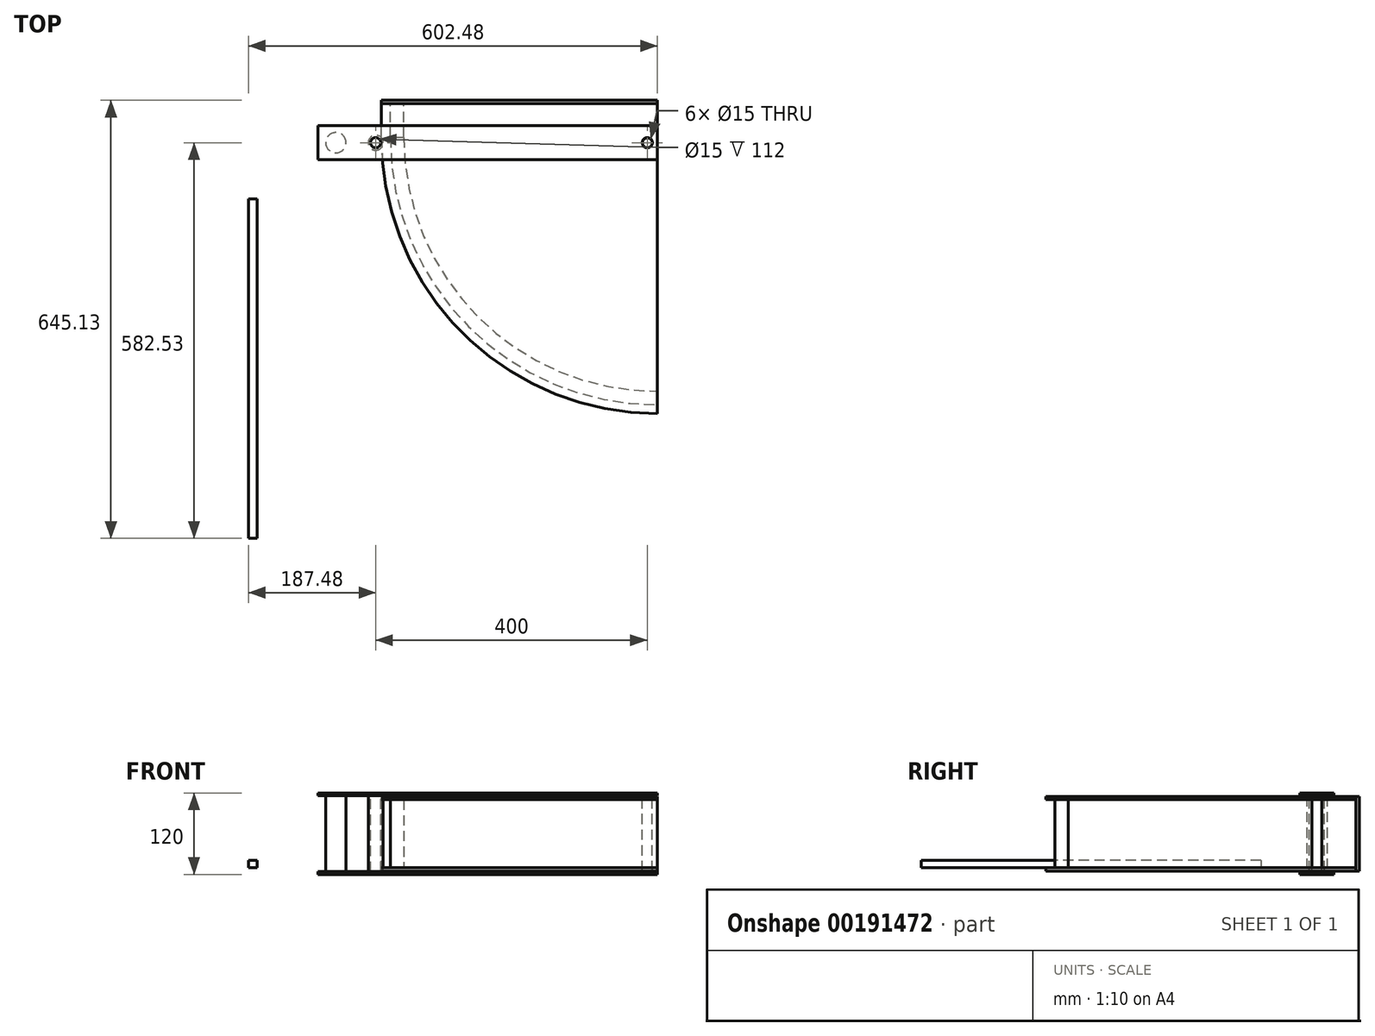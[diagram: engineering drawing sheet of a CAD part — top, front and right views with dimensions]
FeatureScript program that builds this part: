
annotation { "Feature Type Name" : "Feature", "Feature Type Description" : "" }
export const myFeature = defineFeature(function(context is Context, id is Id, definition is map)
    precondition{}
    {
        {
            var Q0;
            Q0=qCreatedBy(makeId("Top.planeOp"),FACE);
            var sketch = newSketch(context, id + "F0", { "sketchPlane" : qUnion([Q0])});
            skLineSegment(sketch, "E0", {"start": v(0, 0) * mm, "end": v(-393.5, 0) * mm});
            skArc(sketch, "E1", {"start": v(-393.5, 0) * mm, "mid": v(-278.25, -278.25) * mm, "end": v(0, -393.5) * mm});
            skLineSegment(sketch, "E2", {"start": v(0, 0) * mm, "end": v(0, -393.5) * mm});
            skArc(sketch, "E3.0", {"start": v(-373.5, 0) * mm, "mid": v(-264.1, -264.1) * mm, "end": v(0, -373.5) * mm});
            skLineSegment(sketch, "E4.top", {"start": v(-393.5, 50) * mm, "end": v(-373.5, 50) * mm});
            skLineSegment(sketch, "E4.left", {"start": v(-393.5, 0) * mm, "end": v(-393.5, 50) * mm});
            skLineSegment(sketch, "E4.right", {"start": v(-373.5, 0) * mm, "end": v(-373.5, 50) * mm});
            skSolve(sketch);
        }
        {
            var Q0;
            {var subQ0=sQuery(id+"F0.wireOp",EDGE,"E1");Q0=makeQuery(id+"F0.imprint","IMPRINT",FACE,{"disambiguationData":[TD([[makeQuery(id+"F0.imprint","IMPRINT",EDGE,{"derivedFrom":subQ0}),1.0]])]});}
            var Q1;
            Q1=makeQuery(id+"F0.imprint","IMPRINT",FACE,{"disambiguationData":[TD([[makeQuery(id+"F0.imprint","IMPRINT",EDGE,{"derivedFrom":sQuery(id+"F0.wireOp",EDGE,"E4.bottom")}),1.0]])]});
            extrude(context, id + "F1", {"entities" : qUnion([Q0, Q1]), "depth" : 100 * mm});
        }
        {
            var Q0;
            Q0=makeQuery(id+"F1.opExtrude","CAP_FACE",FACE,{"disambiguationData":[OSD([sQuery(id+"F0.wireOp",EDGE,"E0"),sQuery(id+"F0.wireOp",EDGE,"E1"),sQuery(id+"F0.wireOp",EDGE,"E2"),sQuery(id+"F0.wireOp",EDGE,"E3.0")])],"isStart":true});
            cPlane(context, id + "F2", {"entities" : qUnion([Q0]), "cplaneType" : CPlaneType.OFFSET, "offset" : 0 * mm, "width" : 150 * mm, "height" : 150 * mm});
        }
        {
            var Q0;
            Q0=qCreatedBy(id+"F2.planeOp",FACE);
            var sketch = newSketch(context, id + "F3", { "sketchPlane" : qUnion([Q0])});
            skLineSegment(sketch, "E5", {"start": v(0, 0) * mm, "end": v(0, 406.5) * mm});
            skLineSegment(sketch, "E6", {"start": v(0, 0) * mm, "end": v(-406.5, 0) * mm});
            skArc(sketch, "E7", {"start": v(0, 393.5) * mm, "mid": v(-278.25, 278.25) * mm, "end": v(-393.5, 0) * mm});
            skArc(sketch, "E8.0", {"start": v(0, 406.5) * mm, "mid": v(-287.44, 287.44) * mm, "end": v(-406.5, 0) * mm});
            skLineSegment(sketch, "E9.bottom", {"start": v(-406.5, 0) * mm, "end": v(0, 0) * mm});
            skLineSegment(sketch, "E9.top", {"start": v(-406.5, -50) * mm, "end": v(0, -50) * mm});
            skLineSegment(sketch, "E9.right", {"start": v(0, 0) * mm, "end": v(0, -50) * mm});
            skLineSegment(sketch, "E10", {"start": v(-406.5, 0) * mm, "end": v(-406.5, -50) * mm});
            skSolve(sketch);
        }
        {
            var Q0;
            Q0=qSketchRegion(id+"F3",true);
            extrude(context, id + "F4", {"entities" : qUnion([Q0]), "depth" : 5 * mm});
        }
        {
            var Q0;
            Q0=makeQuery(id+"F1.opExtrude","CAP_FACE",FACE,{"disambiguationData":[OSD([sQuery(id+"F0.wireOp",EDGE,"E0"),sQuery(id+"F0.wireOp",EDGE,"E1"),sQuery(id+"F0.wireOp",EDGE,"E2"),sQuery(id+"F0.wireOp",EDGE,"E3.0")])],"isStart":false});
            cPlane(context, id + "F5", {"entities" : qUnion([Q0]), "cplaneType" : CPlaneType.OFFSET, "offset" : 0 * mm, "width" : 150 * mm, "height" : 150 * mm});
        }
        {
            var Q0;
            Q0=qCreatedBy(id+"F5.planeOp",FACE);
            var sketch = newSketch(context, id + "F6", { "sketchPlane" : qUnion([Q0])});
            skLineSegment(sketch, "E11", {"start": v(0, 0) * mm, "end": v(0, -393.5) * mm});
            skLineSegment(sketch, "E12", {"start": v(0, 0) * mm, "end": v(-393.5, 0) * mm});
            skArc(sketch, "E13.0", {"start": v(-393.5, 0) * mm, "mid": v(-278.25, -278.25) * mm, "end": v(0, -393.5) * mm});
            skLineSegment(sketch, "E14.bottom", {"start": v(-393.5, 0) * mm, "end": v(0, 0) * mm});
            skLineSegment(sketch, "E14.top", {"start": v(-393.5, 50) * mm, "end": v(0, 50) * mm});
            skLineSegment(sketch, "E14.left", {"start": v(-393.5, 0) * mm, "end": v(-393.5, 50) * mm});
            skLineSegment(sketch, "E14.right", {"start": v(0, 0) * mm, "end": v(0, 50) * mm});
            skLineSegment(sketch, "E15", {"start": v(0, -393.5) * mm, "end": v(0, -406.5) * mm});
            skArc(sketch, "E16", {"start": v(-406.5, 0) * mm, "mid": v(-287.44, -287.44) * mm, "end": v(0, -406.5) * mm});
            skLineSegment(sketch, "E17", {"start": v(-393.5, 0) * mm, "end": v(-406.5, 0) * mm});
            skLineSegment(sketch, "E18", {"start": v(-406.5, 0) * mm, "end": v(-406.5, 50) * mm});
            skLineSegment(sketch, "E19", {"start": v(-406.5, 50) * mm, "end": v(-393.5, 50) * mm});
            skSolve(sketch);
        }
        {
            var Q0;
            Q0=qSketchRegion(id+"F6",true);
            extrude(context, id + "F7", {"entities" : qUnion([Q0]), "depth" : 5 * mm});
        }
        {
            var Q0;
            Q0=makeQuery(id+"F4.opExtrude","SWEPT_FACE",FACE,{"disambiguationData":[OSD([sQuery(id+"F3.wireOp",EDGE,"E9.top")])]});
            cPlane(context, id + "F8", {"entities" : qUnion([Q0]), "cplaneType" : CPlaneType.OFFSET, "offset" : 0 * mm, "width" : 150 * mm, "height" : 150 * mm});
        }
        {
            var Q0;
            Q0=qCreatedBy(id+"F8.planeOp",FACE);
            var sketch = newSketch(context, id + "F9", { "sketchPlane" : qUnion([Q0])});
            skLineSegment(sketch, "E20", {"start": v(0, -5) * mm, "end": v(0, 105) * mm});
            skLineSegment(sketch, "E21", {"start": v(0, -5) * mm, "end": v(406.5, -5) * mm});
            skLineSegment(sketch, "E22", {"start": v(406.5, -5) * mm, "end": v(406.5, 105) * mm});
            skLineSegment(sketch, "E23", {"start": v(406.5, 105) * mm, "end": v(0, 105) * mm});
            skSolve(sketch);
        }
        {
            var Q0;
            Q0=qSketchRegion(id+"F9",true);
            extrude(context, id + "F10", {"entities" : qUnion([Q0]), "depth" : 5.1 * mm});
        }
        {
            var Q0;
            Q0=makeQuery(id+"F7.opExtrude","CAP_FACE",FACE,{"disambiguationData":[OSD([sQuery(id+"F6.wireOp",EDGE,"E11"),sQuery(id+"F6.wireOp",EDGE,"E13.0"),sQuery(id+"F6.wireOp",EDGE,"E14.top"),sQuery(id+"F6.wireOp",EDGE,"E14.left"),sQuery(id+"F6.wireOp",EDGE,"E14.right")])],"isStart":false});
            var sketch = newSketch(context, id + "F11", { "sketchPlane" : qUnion([Q0])});
            skCircle(sketch, "E24", {"center": v(-15, -7.5) * mm, "radius": 7.5 * mm});
            skSolve(sketch);
        }
        {
            var Q0;
            Q0=qSketchRegion(id+"F11",true);
            extrude(context, id + "F12", {"entities" : qUnion([Q0]), "operationType" : NewBodyOperationType.REMOVE, "endBound" : BoundingType.THROUGH_ALL, "oppositeDirection" : true, "depth" : 42 * mm});
        }
        {
            var Q0;
            Q0=makeQuery(id+"F7.opExtrude","CAP_FACE",FACE,{"disambiguationData":[OSD([sQuery(id+"F6.wireOp",EDGE,"E11"),sQuery(id+"F6.wireOp",EDGE,"E13.0"),sQuery(id+"F6.wireOp",EDGE,"E14.top"),sQuery(id+"F6.wireOp",EDGE,"E14.left"),sQuery(id+"F6.wireOp",EDGE,"E14.right")])],"isStart":false});
            cPlane(context, id + "F13", {"entities" : qUnion([Q0]), "cplaneType" : CPlaneType.OFFSET, "offset" : 5 * mm, "width" : 150 * mm, "height" : 150 * mm});
        }
        {
            var Q0;
            Q0=qCreatedBy(id+"F13.planeOp",FACE);
            var sketch = newSketch(context, id + "F14", { "sketchPlane" : qUnion([Q0])});
            skCircle(sketch, "E25", {"center": v(-15, -7.5) * mm, "radius": 7.25 * mm});
            skSolve(sketch);
        }
        {
            var Q0;
            Q0=qSketchRegion(id+"F14",true);
            extrude(context, id + "F15", {"entities" : qUnion([Q0]), "oppositeDirection" : true, "depth" : 120 * mm});
        }
        {
            var Q0;
            Q0=makeQuery(id+"F15.opExtrude","CAP_FACE",FACE,{"disambiguationData":[OSD([sQuery(id+"F14.wireOp",EDGE,"E25")])],"isStart":true});
            cPlane(context, id + "F16", {"entities" : qUnion([Q0]), "cplaneType" : CPlaneType.OFFSET, "offset" : 0 * mm, "width" : 150 * mm, "height" : 150 * mm});
        }
        {
            var Q0;
            Q0=qCreatedBy(id+"F16.planeOp",FACE);
            var sketch = newSketch(context, id + "F17", { "sketchPlane" : qUnion([Q0])});
            skLineSegment(sketch, "E26.bottom", {"start": v(0, -32.5) * mm, "end": v(-500, -32.5) * mm});
            skLineSegment(sketch, "E26.top", {"start": v(0, 17.5) * mm, "end": v(-500, 17.5) * mm});
            skLineSegment(sketch, "E26.left", {"start": v(0, -32.5) * mm, "end": v(0, 17.5) * mm});
            skLineSegment(sketch, "E26.right", {"start": v(-500, -32.5) * mm, "end": v(-500, 17.5) * mm});
            skCircle(sketch, "E27", {"center": v(-15, -7.5) * mm, "radius": 7.5 * mm});
            skCircle(sketch, "E28", {"center": v(-415, -7.5) * mm, "radius": 7.5 * mm});
            skSolve(sketch);
        }
        {
            var Q0;
            Q0=qSketchRegion(id+"F17",true);
            extrude(context, id + "F18", {"entities" : qUnion([Q0]), "operationType" : NewBodyOperationType.ADD, "oppositeDirection" : true, "depth" : 4 * mm});
        }
        {
            var Q0;
            Q0=qCreatedBy(id+"F5.planeOp",FACE);
            cPlane(context, id + "F19", {"entities" : qUnion([Q0]), "cplaneType" : CPlaneType.OFFSET, "offset" : 50 * mm, "oppositeDirection" : true, "width" : 150 * mm, "height" : 150 * mm});
        }
        {
            var Q0;
            Q0=makeQuery(id+"F18.opExtrude","SWEPT_BODY",BODY,{"disambiguationData":[OSD([sQuery(id+"F17.wireOp",EDGE,"E26.bottom"),sQuery(id+"F17.wireOp",EDGE,"E26.top"),sQuery(id+"F17.wireOp",EDGE,"E26.left"),sQuery(id+"F17.wireOp",EDGE,"E26.right"),sQuery(id+"F17.wireOp",EDGE,"E27")])]});
            var Q1;
            Q1=qCreatedBy(id+"F19.planeOp",FACE);
            mirror(context, id + "F20", {"entities" : qUnion([Q0]), "mirrorPlane" : qUnion([Q1])});
        }
        {
            var Q0;
            Q0=makeQuery(id+"F0.imprint","IMPRINT",FACE,{"disambiguationData":[TD([[makeQuery(id+"F0.imprint","IMPRINT",EDGE,{"derivedFrom":sQuery(id+"F0.wireOp",EDGE,"E4.top")}),-1.0]])]});
            extrude(context, id + "F21", {"entities" : qUnion([Q0]), "depth" : 100 * mm});
        }
        {
            var Q0;
            Q0=makeQuery(id+"F20.opPattern","COPY",FACE,{"derivedFrom":makeQuery(id+"F18.opExtrude","CAP_FACE",FACE,{"disambiguationData":[OSD([sQuery(id+"F17.wireOp",EDGE,"E26.bottom"),sQuery(id+"F17.wireOp",EDGE,"E26.top"),sQuery(id+"F17.wireOp",EDGE,"E26.left"),sQuery(id+"F17.wireOp",EDGE,"E26.right"),sQuery(id+"F17.wireOp",EDGE,"E27"),sQuery(id+"F17.wireOp",EDGE,"E28")])],"isStart":false}),"instanceName":"1"});
            var sketch = newSketch(context, id + "F22", { "sketchPlane" : qUnion([Q0])});
            skCircle(sketch, "E29", {"center": v(-473.58, -7.5) * mm, "radius": 15 * mm});
            skPoint(sketch, "E29.centerSnap0", {"position": v(-500, -7.5) * mm});
            skSolve(sketch);
        }
        {
            var Q0;
            Q0=qSketchRegion(id+"F22",true);
            extrude(context, id + "F23", {"entities" : qUnion([Q0]), "endBound" : BoundingType.UP_TO_NEXT, "depth" : 25 * mm});
        }
        {
            var Q0;
            Q0=makeQuery(id+"F18.opExtrude","CAP_FACE",FACE,{"disambiguationData":[OSD([sQuery(id+"F17.wireOp",EDGE,"E26.bottom"),sQuery(id+"F17.wireOp",EDGE,"E26.top"),sQuery(id+"F17.wireOp",EDGE,"E26.left"),sQuery(id+"F17.wireOp",EDGE,"E26.right"),sQuery(id+"F17.wireOp",EDGE,"E27"),sQuery(id+"F17.wireOp",EDGE,"E28")])],"isStart":false});
            var sketch = newSketch(context, id + "F24", { "sketchPlane" : qUnion([Q0])});
            skCircle(sketch, "E30", {"center": v(-415, 7.5) * mm, "radius": 7.5 * mm});
            skCircle(sketch, "E31", {"center": v(-415, 7.5) * mm, "radius": 11 * mm});
            skSolve(sketch);
        }
        {
            var Q0;
            Q0=qSketchRegion(id+"F24",true);
            extrude(context, id + "F25", {"entities" : qUnion([Q0]), "endBound" : BoundingType.UP_TO_NEXT, "depth" : 25 * mm});
        }
        {
            var Q0;
            Q0=qCreatedBy(makeId("Top.planeOp"),FACE);
            var sketch = newSketch(context, id + "F26", { "sketchPlane" : qUnion([Q0])});
            skLineSegment(sketch, "E32.bottom", {"start": v(-602.48, -90.03) * mm, "end": v(-589.48, -90.03) * mm});
            skLineSegment(sketch, "E32.top", {"start": v(-602.48, -590.03) * mm, "end": v(-589.48, -590.03) * mm});
            skLineSegment(sketch, "E32.left", {"start": v(-602.48, -90.03) * mm, "end": v(-602.48, -590.03) * mm});
            skLineSegment(sketch, "E32.right", {"start": v(-589.48, -90.03) * mm, "end": v(-589.48, -590.03) * mm});
            skSolve(sketch);
        }
        {
            var Q0;
            Q0=qSketchRegion(id+"F26",true);
            extrude(context, id + "F27", {"entities" : qUnion([Q0]), "depth" : 11 * mm});
        }
    });
